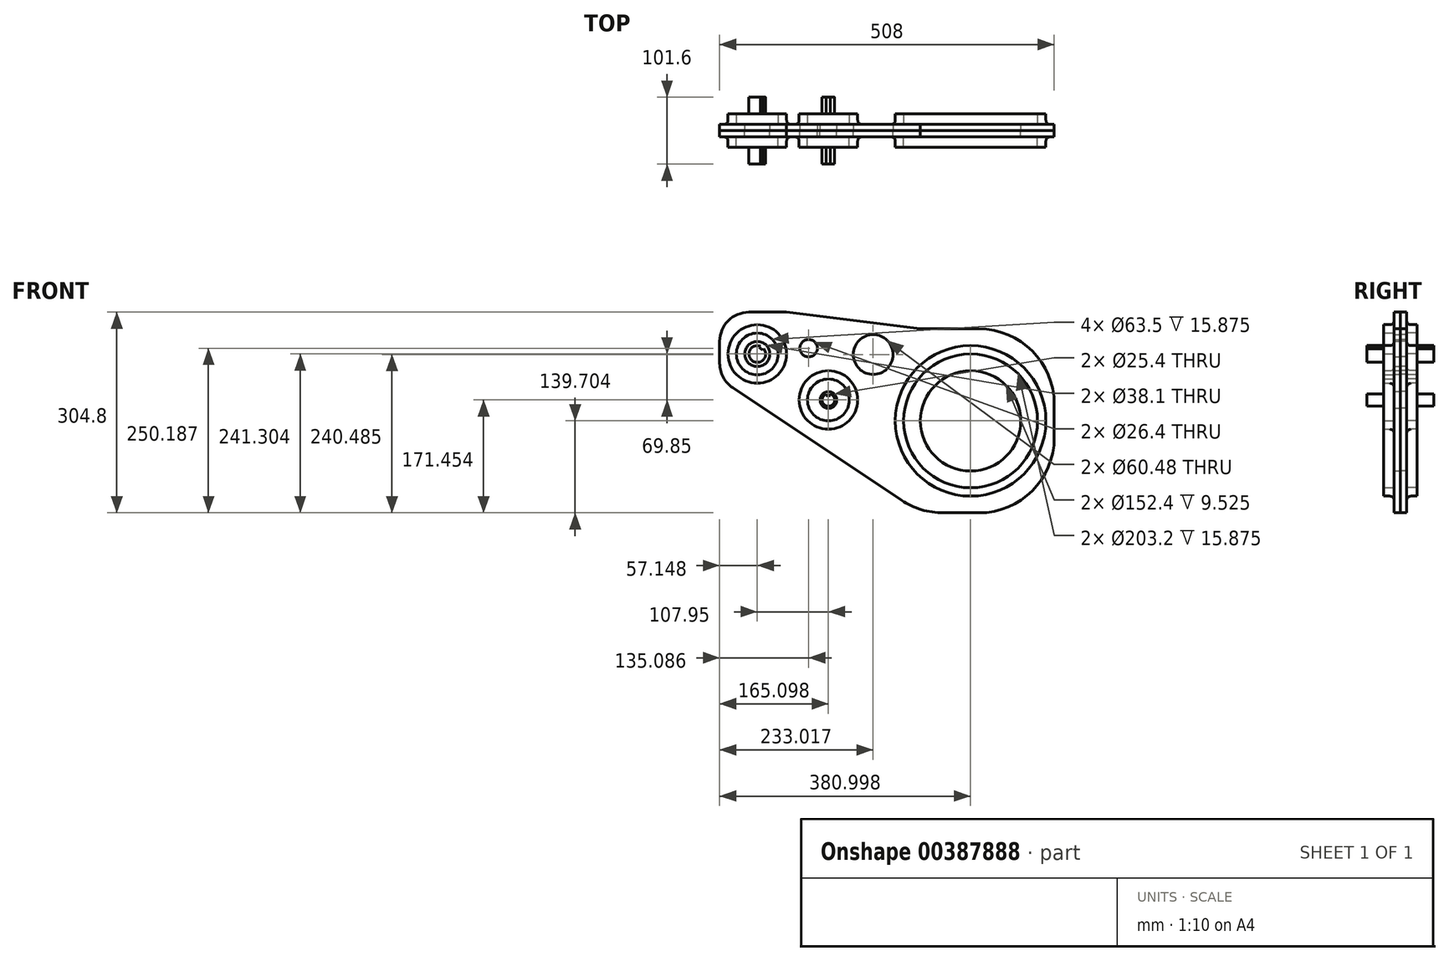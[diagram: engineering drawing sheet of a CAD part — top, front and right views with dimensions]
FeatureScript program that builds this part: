
annotation { "Feature Type Name" : "Feature", "Feature Type Description" : "" }
export const myFeature = defineFeature(function(context is Context, id is Id, definition is map)
    precondition{}
    {
        {
            var Q0;
            Q0=qCreatedBy(makeId("Front.planeOp"),FACE);
            var sketch = newSketch(context, id + "F0", { "sketchPlane" : qUnion([Q0])});
            skLineSegment(sketch, "E0", {"start": v(-208.67, -197.55) * mm, "end": v(-464.88, -26.74) * mm});
            skLineSegment(sketch, "E1", {"start": v(-484.67, 10.24) * mm, "end": v(-484.67, 43.6) * mm});
            skLineSegment(sketch, "E2", {"start": v(-440.22, 88.05) * mm, "end": v(-383.07, 88.05) * mm});
            skLineSegment(sketch, "E3", {"start": v(-383.07, 88.05) * mm, "end": v(-179.87, 62.65) * mm});
            skLineSegment(sketch, "E4", {"start": v(-179.87, 62.65) * mm, "end": v(-90.97, 62.65) * mm});
            skLineSegment(sketch, "E5", {"start": v(23.33, -51.65) * mm, "end": v(23.33, -102.45) * mm});
            skLineSegment(sketch, "E6", {"start": v(-90.97, -216.75) * mm, "end": v(-145.27, -216.75) * mm});
            skCircle(sketch, "E7", {"center": v(-103.67, -77.05) * mm, "radius": 101.6 * mm});
            skCircle(sketch, "E8", {"center": v(-319.57, -45.3) * mm, "radius": 31.75 * mm});
            skCircle(sketch, "E9", {"center": v(-427.52, 24.55) * mm, "radius": 31.75 * mm});
            skCircle(sketch, "E10", {"center": v(-103.67, -77.05) * mm, "radius": 114.3 * mm});
            skCircle(sketch, "E11", {"center": v(-319.57, -45.3) * mm, "radius": 44.45 * mm});
            skCircle(sketch, "E12", {"center": v(-427.52, 24.55) * mm, "radius": 44.45 * mm});
            skCircle(sketch, "E13", {"center": v(-319.57, -45.3) * mm, "radius": 12.7 * mm});
            skCircle(sketch, "E14", {"center": v(-103.67, -77.05) * mm, "radius": 76.2 * mm});
            skCircle(sketch, "E15", {"center": v(-427.52, 24.55) * mm, "radius": 19.05 * mm});
            skPoint(sketch, "E16.visualSharp", {"position": v(23.33, 62.65) * mm});
            skArc(sketch, "E16.filletArc", {"start": v(23.33, -51.65) * mm, "mid": v(-10.15, 29.18) * mm, "end": v(-90.97, 62.65) * mm});
            skPoint(sketch, "E17.visualSharp", {"position": v(23.33, -216.75) * mm});
            skArc(sketch, "E17.filletArc", {"start": v(-90.97, -216.75) * mm, "mid": v(-10.15, -183.27) * mm, "end": v(23.33, -102.45) * mm});
            skPoint(sketch, "E18.visualSharp", {"position": v(-179.87, -216.75) * mm});
            skArc(sketch, "E18.filletArc", {"start": v(-208.67, -197.55) * mm, "mid": v(-178.39, -211.84) * mm, "end": v(-145.27, -216.75) * mm});
            skPoint(sketch, "E19.visualSharp", {"position": v(-484.67, -13.55) * mm});
            skArc(sketch, "E19.filletArc", {"start": v(-484.67, 10.24) * mm, "mid": v(-479.41, -10.73) * mm, "end": v(-464.88, -26.74) * mm});
            skPoint(sketch, "E20.visualSharp", {"position": v(-484.67, 88.05) * mm});
            skArc(sketch, "E20.filletArc", {"start": v(-440.22, 88.05) * mm, "mid": v(-471.65, 75.03) * mm, "end": v(-484.67, 43.6) * mm});
            skCircle(sketch, "E21", {"center": v(-251.65, 23.74) * mm, "radius": 30.24 * mm});
            skCircle(sketch, "E22", {"center": v(-349.58, 33.44) * mm, "radius": 13.2 * mm});
            skSolve(sketch);
        }
        {
            var Q0;
            Q0=makeQuery(id+"F0.imprint","IMPRINT",FACE,{"disambiguationData":[TD([[makeQuery(id+"F0.imprint","IMPRINT",EDGE,{"derivedFrom":sQuery(id+"F0.wireOp",EDGE,"E0")}),-1.0]])]});
            var Q1;
            Q1=makeQuery(id+"F0.imprint","IMPRINT",FACE,{"disambiguationData":[TD([[makeQuery(id+"F0.imprint","IMPRINT",EDGE,{"derivedFrom":sQuery(id+"F0.wireOp",EDGE,"E9")}),-1.0]])]});
            var Q2;
            Q2=makeQuery(id+"F0.imprint","IMPRINT",FACE,{"disambiguationData":[TD([[makeQuery(id+"F0.imprint","IMPRINT",EDGE,{"derivedFrom":sQuery(id+"F0.wireOp",EDGE,"E8")}),-1.0]])]});
            var Q3;
            Q3=makeQuery(id+"F0.imprint","IMPRINT",FACE,{"disambiguationData":[TD([[makeQuery(id+"F0.imprint","IMPRINT",EDGE,{"derivedFrom":sQuery(id+"F0.wireOp",EDGE,"E7")}),-1.0]])]});
            var Q4;
            Q4=makeQuery(id+"F0.imprint","IMPRINT",FACE,{"disambiguationData":[TD([[makeQuery(id+"F0.imprint","IMPRINT",EDGE,{"derivedFrom":sQuery(id+"F0.wireOp",EDGE,"E9")}),1.0]])]});
            var Q5;
            Q5=makeQuery(id+"F0.imprint","IMPRINT",FACE,{"disambiguationData":[TD([[makeQuery(id+"F0.imprint","IMPRINT",EDGE,{"derivedFrom":sQuery(id+"F0.wireOp",EDGE,"E8")}),1.0]])]});
            var Q6;
            Q6=makeQuery(id+"F0.imprint","IMPRINT",FACE,{"disambiguationData":[TD([[makeQuery(id+"F0.imprint","IMPRINT",EDGE,{"derivedFrom":sQuery(id+"F0.wireOp",EDGE,"E7")}),1.0]])]});
            extrude(context, id + "F1", {"entities" : qUnion([Q0, Q1, Q2, Q3, Q4, Q5, Q6]), "depth" : 19.05 * mm});
        }
        {
            var Q0;
            Q0=makeQuery(id+"F0.imprint","IMPRINT",FACE,{"disambiguationData":[TD([[makeQuery(id+"F0.imprint","IMPRINT",EDGE,{"derivedFrom":sQuery(id+"F0.wireOp",EDGE,"E8")}),-1.0]])]});
            var Q1;
            Q1=makeQuery(id+"F0.imprint","IMPRINT",FACE,{"disambiguationData":[TD([[makeQuery(id+"F0.imprint","IMPRINT",EDGE,{"derivedFrom":sQuery(id+"F0.wireOp",EDGE,"E7")}),-1.0]])]});
            var Q2;
            Q2=makeQuery(id+"F0.imprint","IMPRINT",FACE,{"disambiguationData":[TD([[makeQuery(id+"F0.imprint","IMPRINT",EDGE,{"derivedFrom":sQuery(id+"F0.wireOp",EDGE,"E9")}),-1.0]])]});
            extrude(context, id + "F2", {"entities" : qUnion([Q0, Q1, Q2]), "operationType" : NewBodyOperationType.ADD, "depth" : 25.4 * mm});
        }
        {
            var Q0;
            {var subQ0=sQuery(id+"F0.wireOp",EDGE,"E13");Q0=makeQuery(id+"F2.boolean.opBoolean","SPLIT",FACE,{"disambiguationData":[TD([makeQuery(id+"F1.opExtrude","SWEPT_FACE",FACE,{"disambiguationData":[OSD([subQ0])]})])],"derivedFrom":makeQuery(id+"F1.opExtrude","CAP_FACE",FACE,{"disambiguationData":[OSD([sQuery(id+"F0.wireOp",EDGE,"E0"),sQuery(id+"F0.wireOp",EDGE,"E1"),sQuery(id+"F0.wireOp",EDGE,"E2"),sQuery(id+"F0.wireOp",EDGE,"E3"),sQuery(id+"F0.wireOp",EDGE,"E4"),sQuery(id+"F0.wireOp",EDGE,"E5"),sQuery(id+"F0.wireOp",EDGE,"E6"),subQ0,sQuery(id+"F0.wireOp",EDGE,"E14"),sQuery(id+"F0.wireOp",EDGE,"E15")])],"isStart":false})});}
            var Q1;
            {var subQ0=sQuery(id+"F0.wireOp",EDGE,"E2");var subQ1=sQuery(id+"F0.wireOp",EDGE,"E1");var subQ2=sQuery(id+"F0.wireOp",EDGE,"E3");var subQ3=sQuery(id+"F0.wireOp",EDGE,"E0");var subQ4=sQuery(id+"F0.wireOp",EDGE,"E15");var subQ5=sQuery(id+"F0.wireOp",EDGE,"E4");var subQ6=sQuery(id+"F0.wireOp",EDGE,"E5");var subQ7=sQuery(id+"F0.wireOp",EDGE,"E6");Q1=makeQuery(id+"F2.boolean.opBoolean","SPLIT",FACE,{"disambiguationData":[TD([makeQuery(id+"F1.opExtrude","SWEPT_FACE",FACE,{"disambiguationData":[OSD([subQ3])]})])],"derivedFrom":makeQuery(id+"F1.opExtrude","CAP_FACE",FACE,{"disambiguationData":[OSD([subQ3,subQ1,subQ0,subQ2,subQ5,subQ6,subQ7,sQuery(id+"F0.wireOp",EDGE,"E13"),sQuery(id+"F0.wireOp",EDGE,"E14"),subQ4])],"isStart":false})});}
            var Q2;
            {var subQ0=sQuery(id+"F0.wireOp",EDGE,"E14");Q2=makeQuery(id+"F2.boolean.opBoolean","SPLIT",FACE,{"disambiguationData":[TD([makeQuery(id+"F1.opExtrude","SWEPT_FACE",FACE,{"disambiguationData":[OSD([subQ0])]})])],"derivedFrom":makeQuery(id+"F1.opExtrude","CAP_FACE",FACE,{"disambiguationData":[OSD([sQuery(id+"F0.wireOp",EDGE,"E0"),sQuery(id+"F0.wireOp",EDGE,"E1"),sQuery(id+"F0.wireOp",EDGE,"E2"),sQuery(id+"F0.wireOp",EDGE,"E3"),sQuery(id+"F0.wireOp",EDGE,"E4"),sQuery(id+"F0.wireOp",EDGE,"E5"),sQuery(id+"F0.wireOp",EDGE,"E6"),sQuery(id+"F0.wireOp",EDGE,"E13"),subQ0,sQuery(id+"F0.wireOp",EDGE,"E15")])],"isStart":false})});}
            var Q3;
            {var subQ0=sQuery(id+"F0.wireOp",EDGE,"E15");Q3=makeQuery(id+"F2.boolean.opBoolean","SPLIT",FACE,{"disambiguationData":[TD([makeQuery(id+"F1.opExtrude","SWEPT_FACE",FACE,{"disambiguationData":[OSD([subQ0])]})])],"derivedFrom":makeQuery(id+"F1.opExtrude","CAP_FACE",FACE,{"disambiguationData":[OSD([sQuery(id+"F0.wireOp",EDGE,"E0"),sQuery(id+"F0.wireOp",EDGE,"E1"),sQuery(id+"F0.wireOp",EDGE,"E2"),sQuery(id+"F0.wireOp",EDGE,"E3"),sQuery(id+"F0.wireOp",EDGE,"E4"),sQuery(id+"F0.wireOp",EDGE,"E5"),sQuery(id+"F0.wireOp",EDGE,"E6"),sQuery(id+"F0.wireOp",EDGE,"E13"),sQuery(id+"F0.wireOp",EDGE,"E14"),subQ0])],"isStart":false})});}
            extrude(context, id + "F3", {"entities" : qUnion([Q0, Q1, Q2, Q3]), "operationType" : NewBodyOperationType.REMOVE, "oppositeDirection" : true, "depth" : 9.52 * mm});
        }
        {
            var Q0;
            Q0=makeQuery(id+"F3.boolean.opBoolean","COPY",EDGE,{"derivedFrom":makeQuery(id+"F3.opExtrude","CAP_EDGE",EDGE,{"disambiguationData":[OSD([sQuery(id+"F0.wireOp",EDGE,"E0"),sQuery(id+"F0.wireOp",EDGE,"E1"),sQuery(id+"F0.wireOp",EDGE,"E2"),sQuery(id+"F0.wireOp",EDGE,"E3"),sQuery(id+"F0.wireOp",EDGE,"E4"),sQuery(id+"F0.wireOp",EDGE,"E5"),sQuery(id+"F0.wireOp",EDGE,"E6"),sQuery(id+"F0.wireOp",EDGE,"E10"),sQuery(id+"F0.wireOp",EDGE,"E13"),sQuery(id+"F0.wireOp",EDGE,"E14"),sQuery(id+"F0.wireOp",EDGE,"E15")])],"isStart":false})});
            var Q1;
            Q1=makeQuery(id+"F3.boolean.opBoolean","COPY",EDGE,{"derivedFrom":makeQuery(id+"F3.opExtrude","CAP_EDGE",EDGE,{"disambiguationData":[OSD([sQuery(id+"F0.wireOp",EDGE,"E0"),sQuery(id+"F0.wireOp",EDGE,"E1"),sQuery(id+"F0.wireOp",EDGE,"E2"),sQuery(id+"F0.wireOp",EDGE,"E3"),sQuery(id+"F0.wireOp",EDGE,"E4"),sQuery(id+"F0.wireOp",EDGE,"E5"),sQuery(id+"F0.wireOp",EDGE,"E6"),sQuery(id+"F0.wireOp",EDGE,"E11"),sQuery(id+"F0.wireOp",EDGE,"E13"),sQuery(id+"F0.wireOp",EDGE,"E14"),sQuery(id+"F0.wireOp",EDGE,"E15")])],"isStart":false})});
            var Q2;
            Q2=makeQuery(id+"F3.boolean.opBoolean","COPY",EDGE,{"derivedFrom":makeQuery(id+"F3.opExtrude","CAP_EDGE",EDGE,{"disambiguationData":[OSD([sQuery(id+"F0.wireOp",EDGE,"E0"),sQuery(id+"F0.wireOp",EDGE,"E1"),sQuery(id+"F0.wireOp",EDGE,"E2"),sQuery(id+"F0.wireOp",EDGE,"E3"),sQuery(id+"F0.wireOp",EDGE,"E4"),sQuery(id+"F0.wireOp",EDGE,"E5"),sQuery(id+"F0.wireOp",EDGE,"E6"),sQuery(id+"F0.wireOp",EDGE,"E12"),sQuery(id+"F0.wireOp",EDGE,"E13"),sQuery(id+"F0.wireOp",EDGE,"E14"),sQuery(id+"F0.wireOp",EDGE,"E15")])],"isStart":false})});
            fillet(context, id + "F4", {"entities" : qUnion([Q0, Q1, Q2]), "radius" : 6.35 * mm, "tangentPropagation" : true, "allowEdgeOverflow" : false});
        }
        {
            var Q0;
            Q0=makeQuery(id+"F1.opExtrude","SWEPT_BODY",BODY,{"disambiguationData":[OSD([sQuery(id+"F0.wireOp",EDGE,"E0"),sQuery(id+"F0.wireOp",EDGE,"E1"),sQuery(id+"F0.wireOp",EDGE,"E2"),sQuery(id+"F0.wireOp",EDGE,"E3"),sQuery(id+"F0.wireOp",EDGE,"E4"),sQuery(id+"F0.wireOp",EDGE,"E5"),sQuery(id+"F0.wireOp",EDGE,"E6"),sQuery(id+"F0.wireOp",EDGE,"E13"),sQuery(id+"F0.wireOp",EDGE,"E14"),sQuery(id+"F0.wireOp",EDGE,"E15"),sQuery(id+"F0.wireOp",EDGE,"E16.filletArc"),sQuery(id+"F0.wireOp",EDGE,"E17.filletArc"),sQuery(id+"F0.wireOp",EDGE,"E18.filletArc"),sQuery(id+"F0.wireOp",EDGE,"E19.filletArc"),sQuery(id+"F0.wireOp",EDGE,"E20.filletArc"),sQuery(id+"F0.wireOp",EDGE,"E21"),sQuery(id+"F0.wireOp",EDGE,"E22")])]});
            transform(context, id + "F5", {"entities" : qUnion([Q0]), "transformType" : TransformType.TRANSLATION_3D, "dx" : 0 * mm, "dy" : 0 * mm, "dz" : 0 * mm, "makeCopy" : true});
        }
        {
            var Q0;
            Q0=makeQuery(id+"F5.opPattern","COPY",BODY,{"derivedFrom":makeQuery(id+"F1.opExtrude","SWEPT_BODY",BODY,{"disambiguationData":[OSD([sQuery(id+"F0.wireOp",EDGE,"E0"),sQuery(id+"F0.wireOp",EDGE,"E1"),sQuery(id+"F0.wireOp",EDGE,"E2"),sQuery(id+"F0.wireOp",EDGE,"E3"),sQuery(id+"F0.wireOp",EDGE,"E4"),sQuery(id+"F0.wireOp",EDGE,"E5"),sQuery(id+"F0.wireOp",EDGE,"E6"),sQuery(id+"F0.wireOp",EDGE,"E13"),sQuery(id+"F0.wireOp",EDGE,"E14"),sQuery(id+"F0.wireOp",EDGE,"E15"),sQuery(id+"F0.wireOp",EDGE,"E16.filletArc"),sQuery(id+"F0.wireOp",EDGE,"E17.filletArc"),sQuery(id+"F0.wireOp",EDGE,"E18.filletArc"),sQuery(id+"F0.wireOp",EDGE,"E19.filletArc"),sQuery(id+"F0.wireOp",EDGE,"E20.filletArc"),sQuery(id+"F0.wireOp",EDGE,"E21"),sQuery(id+"F0.wireOp",EDGE,"E22")])]}),"instanceName":"1"});
            deleteBodies(context, id + "F6", {"entities" : qUnion([Q0])});
        }
        {
            var Q0;
            Q0=makeQuery(id+"F1.opExtrude","SWEPT_BODY",BODY,{"disambiguationData":[OSD([sQuery(id+"F0.wireOp",EDGE,"E0"),sQuery(id+"F0.wireOp",EDGE,"E1"),sQuery(id+"F0.wireOp",EDGE,"E2"),sQuery(id+"F0.wireOp",EDGE,"E3"),sQuery(id+"F0.wireOp",EDGE,"E4"),sQuery(id+"F0.wireOp",EDGE,"E5"),sQuery(id+"F0.wireOp",EDGE,"E6"),sQuery(id+"F0.wireOp",EDGE,"E13"),sQuery(id+"F0.wireOp",EDGE,"E14"),sQuery(id+"F0.wireOp",EDGE,"E15"),sQuery(id+"F0.wireOp",EDGE,"E16.filletArc"),sQuery(id+"F0.wireOp",EDGE,"E17.filletArc"),sQuery(id+"F0.wireOp",EDGE,"E18.filletArc"),sQuery(id+"F0.wireOp",EDGE,"E19.filletArc"),sQuery(id+"F0.wireOp",EDGE,"E20.filletArc"),sQuery(id+"F0.wireOp",EDGE,"E21"),sQuery(id+"F0.wireOp",EDGE,"E22")])]});
            var Q1;
            Q1=qCreatedBy(makeId("Front.planeOp"),FACE);
            mirror(context, id + "F7", {"entities" : qUnion([Q0]), "mirrorPlane" : qUnion([Q1])});
        }
        {
            var Q0;
            Q0=qCreatedBy(makeId("Front.planeOp"),FACE);
            var sketch = newSketch(context, id + "F8", { "sketchPlane" : qUnion([Q0])});
            skCircle(sketch, "E23", {"center": v(-427.52, 24.55) * mm, "radius": 12.7 * mm});
            skPoint(sketch, "E24.middle", {"position": v(-420.09, 34.85) * mm});
            skLineSegment(sketch, "E25", {"start": v(-420.09, 34.85) * mm, "end": v(-427.52, 24.55) * mm});
            skLineSegment(sketch, "E26", {"start": v(-419.37, 30.42) * mm, "end": v(-417.75, 32.66) * mm});
            skLineSegment(sketch, "E27", {"start": v(-424.52, 34.13) * mm, "end": v(-422.9, 36.38) * mm});
            skLineSegment(sketch, "E28", {"start": v(-419.37, 30.42) * mm, "end": v(-424.52, 34.13) * mm});
            skSolve(sketch);
        }
        {
            var Q0;
            {var subQ1=sQuery(id+"F8.wireOp",EDGE,"E26");Q0=makeQuery(id+"F8.imprint","IMPRINT",FACE,{"disambiguationData":[TD([[makeQuery(id+"F8.imprint","IMPRINT",EDGE,{"derivedFrom":subQ1}),-1.0]])]});}
            extrude(context, id + "F9", {"entities" : qUnion([Q0]), "endBound" : BoundingType.SYMMETRIC, "depth" : 101.6 * mm});
        }
        {
            var Q0;
            Q0=qCreatedBy(makeId("Front.planeOp"),FACE);
            var sketch = newSketch(context, id + "F10", { "sketchPlane" : qUnion([Q0])});
            skCircle(sketch, "E29", {"center": v(-319.57, -45.3) * mm, "radius": 9.53 * mm});
            skLineSegment(sketch, "E30", {"start": v(-319.57, -45.3) * mm, "end": v(-319.57, -35.77) * mm});
            skLineSegment(sketch, "E31", {"start": v(-319.57, -38.95) * mm, "end": v(-316.4, -38.95) * mm});
            skLineSegment(sketch, "E32", {"start": v(-316.4, -38.95) * mm, "end": v(-316.4, -36.32) * mm});
            skLineSegment(sketch, "E33", {"start": v(-319.57, -38.95) * mm, "end": v(-322.75, -38.95) * mm});
            skLineSegment(sketch, "E34", {"start": v(-322.75, -38.95) * mm, "end": v(-322.75, -36.32) * mm});
            skSolve(sketch);
        }
        {
            var Q0;
            Q0=makeQuery(id+"F10.imprint","IMPRINT",FACE,{"disambiguationData":[TD([[makeQuery(id+"F10.imprint","IMPRINT",EDGE,{"derivedFrom":sQuery(id+"F10.wireOp",EDGE,"E31")}),-1.0]])]});
            extrude(context, id + "F11", {"entities" : qUnion([Q0]), "endBound" : BoundingType.SYMMETRIC, "depth" : 101.6 * mm});
        }
    });
